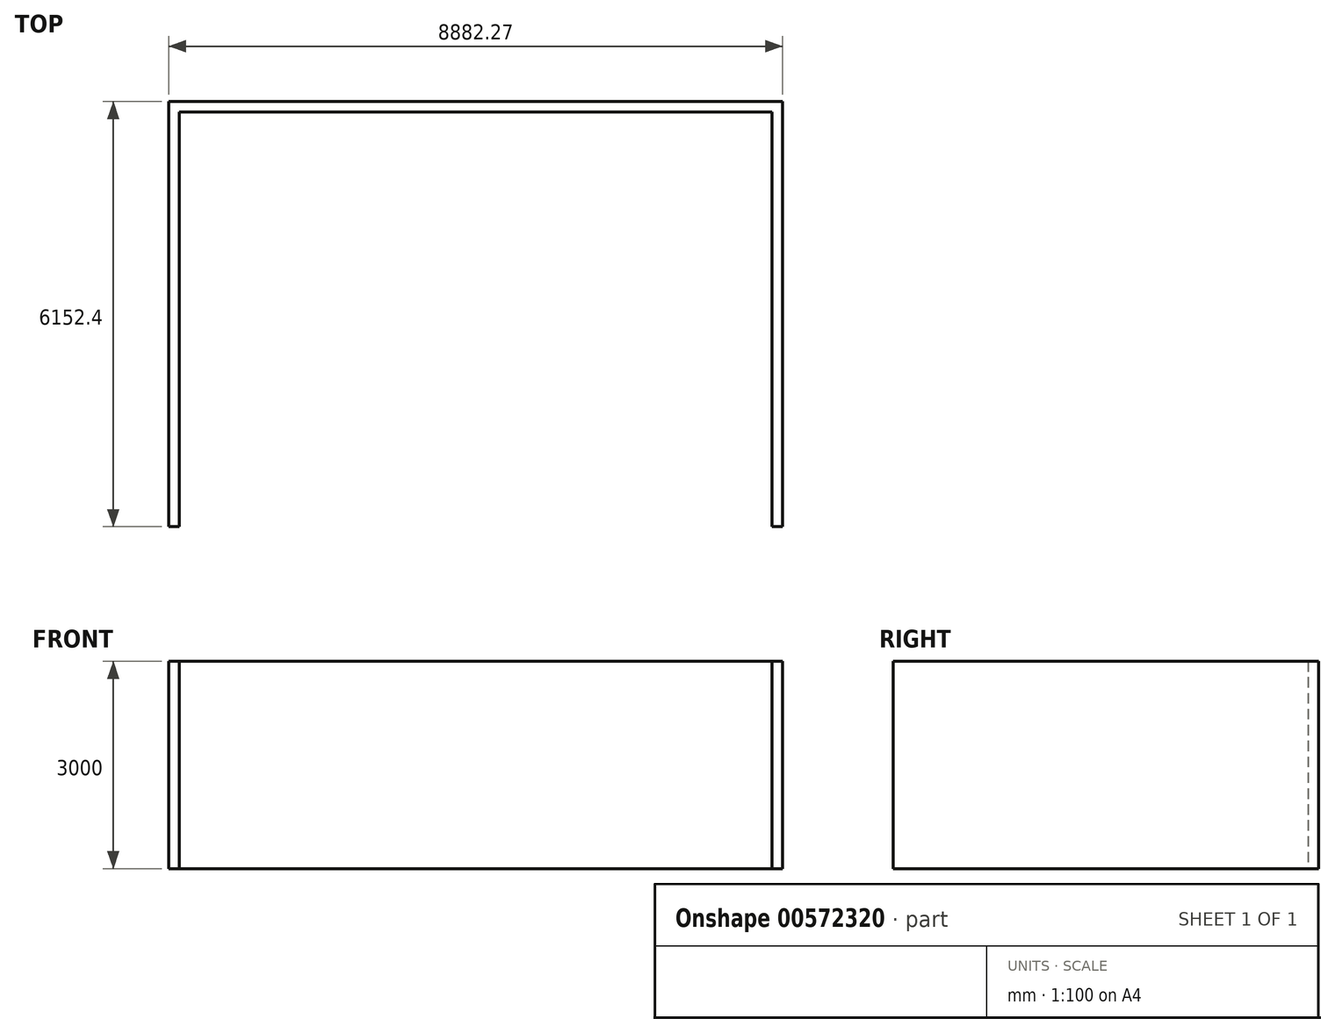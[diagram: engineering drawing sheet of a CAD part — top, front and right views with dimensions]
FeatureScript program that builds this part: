
annotation { "Feature Type Name" : "Feature", "Feature Type Description" : "" }
export const myFeature = defineFeature(function(context is Context, id is Id, definition is map)
    precondition{}
    {
        {
            var Q0;
            Q0=qCreatedBy(makeId("Top.planeOp"),FACE);
            var sketch = newSketch(context, id + "F0", { "sketchPlane" : qUnion([Q0])});
            skLineSegment(sketch, "E0", {"start": v(2645.54, -1227.66) * mm, "end": v(2645.54, 474.14) * mm});
            skLineSegment(sketch, "E1", {"start": v(2645.54, 474.14) * mm, "end": v(4186.83, 474.14) * mm});
            skLineSegment(sketch, "E2", {"start": v(4186.83, 474.14) * mm, "end": v(5204.59, -238.35) * mm});
            skLineSegment(sketch, "E3", {"start": v(5204.59, -238.35) * mm, "end": v(5204.59, -2140.25) * mm});
            skLineSegment(sketch, "E4", {"start": v(5204.59, -1302.05) * mm, "end": v(4417.19, -1302.05) * mm});
            skLineSegment(sketch, "E5", {"start": v(4417.19, -1302.05) * mm, "end": v(4417.19, -2140.25) * mm});
            skLineSegment(sketch, "E6", {"start": v(2645.54, -1227.66) * mm, "end": v(3458.34, -1227.66) * mm});
            skLineSegment(sketch, "E7", {"start": v(3458.34, -1227.66) * mm, "end": v(3458.34, -1354.66) * mm});
            skLineSegment(sketch, "E8", {"start": v(3458.34, -1354.66) * mm, "end": v(2489.79, -1354.66) * mm});
            skLineSegment(sketch, "E9", {"start": v(2489.79, -1227.66) * mm, "end": v(2489.79, -6410.36) * mm});
            skLineSegment(sketch, "E10", {"start": v(4417.19, -2140.25) * mm, "end": v(4544.19, -2140.25) * mm});
            skLineSegment(sketch, "E11", {"start": v(4544.19, -2140.25) * mm, "end": v(4544.19, -1431.88) * mm});
            skLineSegment(sketch, "E12", {"start": v(4417.19, -1431.88) * mm, "end": v(5204.59, -1431.88) * mm});
            skLineSegment(sketch, "E13", {"start": v(4780.3, -2140.25) * mm, "end": v(5334.59, -2140.25) * mm});
            skLineSegment(sketch, "E14", {"start": v(5334.59, -2140.25) * mm, "end": v(5334.59, -170.67) * mm});
            skLineSegment(sketch, "E15", {"start": v(4986.53, -4821.76) * mm, "end": v(7214.19, -6283.36) * mm});
            skLineSegment(sketch, "E16", {"start": v(7214.19, -6283.36) * mm, "end": v(9652.59, -6283.36) * mm});
            skLineSegment(sketch, "E17", {"start": v(9652.59, -6283.36) * mm, "end": v(9652.59, 1812.9) * mm});
            skLineSegment(sketch, "E18", {"start": v(9652.59, 1812.9) * mm, "end": v(8541.34, 1812.9) * mm});
            skLineSegment(sketch, "E19", {"start": v(8541.34, 1812.9) * mm, "end": v(8541.34, 5165.7) * mm});
            skLineSegment(sketch, "E20", {"start": v(8541.34, 5165.7) * mm, "end": v(7121.46, 5903.66) * mm});
            skLineSegment(sketch, "E21", {"start": v(7121.46, 5903.66) * mm, "end": v(5406.96, 5903.66) * mm});
            skLineSegment(sketch, "E22", {"start": v(5406.96, 5903.66) * mm, "end": v(4807.54, 4849.3) * mm});
            skLineSegment(sketch, "E23", {"start": v(4807.54, 4849.3) * mm, "end": v(4807.54, 3560.24) * mm});
            skLineSegment(sketch, "E24", {"start": v(4807.54, 3560.24) * mm, "end": v(-7773.83, 3560.24) * mm});
            skLineSegment(sketch, "E25", {"start": v(5334.59, -170.67) * mm, "end": v(4232.1, 601.14) * mm});
            skLineSegment(sketch, "E26", {"start": v(4232.1, 601.14) * mm, "end": v(97.26, 601.14) * mm});
            skLineSegment(sketch, "E27.bottom", {"start": v(4232.1, 1693.34) * mm, "end": v(5822.02, 1693.34) * mm});
            skLineSegment(sketch, "E27.top", {"start": v(4232.1, 1515.54) * mm, "end": v(5822.02, 1515.54) * mm});
            skLineSegment(sketch, "E27.left", {"start": v(4232.1, 1693.34) * mm, "end": v(4232.1, 1515.54) * mm});
            skLineSegment(sketch, "E27.right", {"start": v(5822.02, 1693.34) * mm, "end": v(5822.02, 1515.54) * mm});
            skLineSegment(sketch, "E28", {"start": v(97.26, 601.14) * mm, "end": v(-662.53, -46.43) * mm});
            skLineSegment(sketch, "E29", {"start": v(-662.53, -46.43) * mm, "end": v(-662.53, -888.34) * mm});
            skLineSegment(sketch, "E30", {"start": v(-662.53, -888.34) * mm, "end": v(-241.43, -1354.66) * mm});
            skLineSegment(sketch, "E31", {"start": v(2518.54, -1354.66) * mm, "end": v(1140.26, -1354.66) * mm});
            skPoint(sketch, "E32.orphan", {"position": v(-288.93, -1302.05) * mm});
            skLineSegment(sketch, "E33", {"start": v(2518.54, -1227.66) * mm, "end": v(1140.26, -1227.66) * mm});
            skLineSegment(sketch, "E34", {"start": v(-185, -1227.66) * mm, "end": v(-536.37, -838.55) * mm});
            skLineSegment(sketch, "E35", {"start": v(-536.37, -838.55) * mm, "end": v(-536.37, -105.77) * mm});
            skLineSegment(sketch, "E36", {"start": v(-536.37, -105.77) * mm, "end": v(144.04, 474.14) * mm});
            skLineSegment(sketch, "E37", {"start": v(144.04, 474.14) * mm, "end": v(2645.54, 474.14) * mm});
            skLineSegment(sketch, "E38", {"start": v(2518.54, 474.14) * mm, "end": v(2518.54, -6283.36) * mm});
            skLineSegment(sketch, "E39", {"start": v(4986.53, -4821.76) * mm, "end": v(2489.79, -4821.76) * mm});
            skLineSegment(sketch, "E40", {"start": v(-7773.83, -6283.36) * mm, "end": v(-7773.83, -4530.76) * mm});
            skLineSegment(sketch, "E41", {"start": v(-7773.83, -4530.76) * mm, "end": v(-6943.99, -4530.76) * mm});
            skLineSegment(sketch, "E42", {"start": v(-6943.99, -4530.76) * mm, "end": v(-6943.99, -3444.9) * mm});
            skLineSegment(sketch, "E43", {"start": v(-2809.3, -3444.9) * mm, "end": v(-7773.83, -3444.9) * mm});
            skLineSegment(sketch, "E44", {"start": v(-7773.83, -3444.9) * mm, "end": v(-7773.83, 3560.24) * mm});
            skLineSegment(sketch, "E45", {"start": v(97.26, 601.14) * mm, "end": v(144.04, 474.14) * mm});
            skLineSegment(sketch, "E46", {"start": v(-662.53, -46.43) * mm, "end": v(-536.37, -105.77) * mm});
            skLineSegment(sketch, "E47", {"start": v(-662.53, -888.34) * mm, "end": v(-536.37, -838.55) * mm});
            skLineSegment(sketch, "E48", {"start": v(-241.43, -1354.66) * mm, "end": v(-185, -1227.66) * mm});
            skLineSegment(sketch, "E49", {"start": v(4186.83, 474.14) * mm, "end": v(4232.1, 601.14) * mm});
            skLineSegment(sketch, "E50", {"start": v(5204.59, -238.35) * mm, "end": v(5334.59, -170.67) * mm});
            skLineSegment(sketch, "E51", {"start": v(485.77, -1354.66) * mm, "end": v(485.77, -1227.66) * mm});
            skLineSegment(sketch, "E52", {"start": v(1140.26, -1227.66) * mm, "end": v(1140.26, -1354.66) * mm});
            skPoint(sketch, "E52.endSnap0", {"position": v(1138.55, -1354.66) * mm});
            skLineSegment(sketch, "E53.trimOffspring", {"start": v(485.77, -1227.66) * mm, "end": v(-185, -1227.66) * mm});
            skLineSegment(sketch, "E54.trimOffspring", {"start": v(485.77, -1354.66) * mm, "end": v(-241.43, -1354.66) * mm});
            skLineSegment(sketch, "E55.0", {"start": v(4944.59, -4948.76) * mm, "end": v(2489.79, -4948.76) * mm});
            skLineSegment(sketch, "E55.1", {"start": v(-7900.83, -6410.36) * mm, "end": v(-7900.83, -4403.76) * mm});
            skLineSegment(sketch, "E55.2", {"start": v(-7900.83, -155.6) * mm, "end": v(-7900.83, 3687.24) * mm});
            skLineSegment(sketch, "E55.3", {"start": v(4680.54, 3687.24) * mm, "end": v(-7900.83, 3687.24) * mm});
            skLineSegment(sketch, "E55.4", {"start": v(9779.59, -6410.36) * mm, "end": v(9779.59, 1939.9) * mm});
            skLineSegment(sketch, "E55.5", {"start": v(6916.19, -6410.36) * mm, "end": v(9779.59, -6410.36) * mm});
            skLineSegment(sketch, "E55.8", {"start": v(9779.59, 1939.9) * mm, "end": v(8668.34, 1939.9) * mm});
            skLineSegment(sketch, "E55.9", {"start": v(8668.34, 1939.9) * mm, "end": v(8668.34, 5242.81) * mm});
            skLineSegment(sketch, "E55.10", {"start": v(8668.34, 5242.81) * mm, "end": v(7152.5, 6030.66) * mm});
            skLineSegment(sketch, "E55.11", {"start": v(7152.5, 6030.66) * mm, "end": v(5333.07, 6030.66) * mm});
            skLineSegment(sketch, "E55.12", {"start": v(5333.07, 6030.66) * mm, "end": v(4680.54, 4882.87) * mm});
            skLineSegment(sketch, "E55.13", {"start": v(4680.54, 4882.87) * mm, "end": v(4680.54, 3687.24) * mm});
            skLineSegment(sketch, "E56.0", {"start": v(-2809.3, -3571.9) * mm, "end": v(-7900.83, -3571.9) * mm});
            skLineSegment(sketch, "E56.1", {"start": v(-7070.99, -4403.76) * mm, "end": v(-7070.99, -3571.9) * mm});
            skLineSegment(sketch, "E56.2", {"start": v(-7900.83, -4403.76) * mm, "end": v(-7070.99, -4403.76) * mm});
            skLineSegment(sketch, "E57.trimOffspring", {"start": v(-7900.83, -3571.9) * mm, "end": v(-7900.83, -155.6) * mm});
            skLineSegment(sketch, "E58", {"start": v(-2682.3, 3560.24) * mm, "end": v(-2682.3, 1046.56) * mm});
            skLineSegment(sketch, "E59", {"start": v(-2682.3, 1046.56) * mm, "end": v(-2903.72, 1046.56) * mm});
            skLineSegment(sketch, "E60", {"start": v(-3749.48, 1173.56) * mm, "end": v(-3749.48, -282.6) * mm});
            skLineSegment(sketch, "E61", {"start": v(-3749.48, -155.6) * mm, "end": v(-3665.72, -155.6) * mm});
            skLineSegment(sketch, "E62", {"start": v(-2682.3, -155.6) * mm, "end": v(-2682.3, -4527.58) * mm});
            skLineSegment(sketch, "E63.0", {"start": v(-2809.3, -155.6) * mm, "end": v(-2809.3, -4527.58) * mm});
            skLineSegment(sketch, "E63.1", {"start": v(-2809.3, 3485.85) * mm, "end": v(-2809.3, 1046.56) * mm});
            skLineSegment(sketch, "E63.2", {"start": v(-2809.3, 1173.56) * mm, "end": v(-2903.72, 1173.56) * mm});
            skLineSegment(sketch, "E63.3", {"start": v(-3876.48, 1173.56) * mm, "end": v(-3876.48, -282.6) * mm});
            skLineSegment(sketch, "E63.4", {"start": v(-3876.48, -282.6) * mm, "end": v(-3665.72, -282.6) * mm});
            skLineSegment(sketch, "E64", {"start": v(-3876.48, 445.47) * mm, "end": v(-7773.83, 445.47) * mm});
            skLineSegment(sketch, "E65", {"start": v(-7773.83, 572.47) * mm, "end": v(-3876.48, 572.47) * mm});
            skLineSegment(sketch, "E66", {"start": v(-5355.07, -3571.9) * mm, "end": v(-5355.07, -4530.76) * mm});
            skLineSegment(sketch, "E67", {"start": v(-5355.07, -4530.76) * mm, "end": v(-5228.07, -4530.76) * mm});
            skLineSegment(sketch, "E68", {"start": v(-5228.07, -4530.76) * mm, "end": v(-5228.07, -3571.9) * mm});
            skLineSegment(sketch, "E69", {"start": v(-2809.3, -4527.58) * mm, "end": v(-2682.3, -4527.58) * mm});
            skLineSegment(sketch, "E70", {"start": v(-2809.3, -5232.43) * mm, "end": v(-2682.3, -5232.43) * mm});
            skLineSegment(sketch, "E71.trimOffspring", {"start": v(-2682.3, -5232.43) * mm, "end": v(-2682.3, -6283.36) * mm});
            skLineSegment(sketch, "E72.trimOffspring", {"start": v(-2809.3, -5232.43) * mm, "end": v(-2809.3, -6283.36) * mm});
            skLineSegment(sketch, "E73", {"start": v(-3665.72, 1173.56) * mm, "end": v(-3665.72, 1046.56) * mm});
            skLineSegment(sketch, "E74", {"start": v(-2903.72, 1173.56) * mm, "end": v(-2903.72, 1046.56) * mm});
            skLineSegment(sketch, "E75.trimOffspring", {"start": v(-3665.72, 1173.56) * mm, "end": v(-3876.48, 1173.56) * mm});
            skLineSegment(sketch, "E76.trimOffspring", {"start": v(-3665.72, 1046.56) * mm, "end": v(-3749.48, 1046.56) * mm});
            skLineSegment(sketch, "E77.trimOffspring", {"start": v(-2903.72, -155.6) * mm, "end": v(-2682.3, -155.6) * mm});
            skLineSegment(sketch, "E78.trimOffspring", {"start": v(-2903.72, -282.6) * mm, "end": v(-2809.3, -282.6) * mm});
            skLineSegment(sketch, "E79.trimOffspring", {"start": v(-2903.72, -155.6) * mm, "end": v(-2903.72, -282.6) * mm});
            skLineSegment(sketch, "E80.trimOffspring", {"start": v(-3665.72, -155.6) * mm, "end": v(-3665.72, -282.6) * mm});
            skLineSegment(sketch, "E81", {"start": v(-2682.3, 1227.1) * mm, "end": v(-867.36, 1227.1) * mm});
            skLineSegment(sketch, "E82", {"start": v(1803.51, 1227.1) * mm, "end": v(2694.47, 1951.7) * mm});
            skLineSegment(sketch, "E83", {"start": v(2694.47, 1951.7) * mm, "end": v(2694.47, 2417.7) * mm});
            skLineSegment(sketch, "E84.0", {"start": v(2567.47, 2012.12) * mm, "end": v(2567.47, 2417.7) * mm});
            skLineSegment(sketch, "E84.1", {"start": v(1758.39, 1354.1) * mm, "end": v(2567.47, 2012.12) * mm});
            skLineSegment(sketch, "E84.2", {"start": v(-2666.54, 1354.1) * mm, "end": v(-867.36, 1354.1) * mm});
            skLineSegment(sketch, "E85", {"start": v(2567.47, 3179.7) * mm, "end": v(2694.47, 3179.7) * mm});
            skLineSegment(sketch, "E86", {"start": v(2567.47, 2417.7) * mm, "end": v(2694.47, 2417.7) * mm});
            skLineSegment(sketch, "E87.trimOffspring", {"start": v(2694.47, 3179.7) * mm, "end": v(2694.47, 3560.24) * mm});
            skLineSegment(sketch, "E88.trimOffspring", {"start": v(2567.47, 3179.7) * mm, "end": v(2567.47, 3485.85) * mm});
            skLineSegment(sketch, "E89", {"start": v(529.73, 3560.24) * mm, "end": v(529.73, 1354.1) * mm});
            skLineSegment(sketch, "E90.0", {"start": v(402.73, 3485.85) * mm, "end": v(402.73, 1354.1) * mm});
            skLineSegment(sketch, "E91", {"start": v(-867.36, 1354.1) * mm, "end": v(-867.36, 1227.1) * mm});
            skLineSegment(sketch, "E92", {"start": v(-105.36, 1354.1) * mm, "end": v(-105.36, 1227.1) * mm});
            skLineSegment(sketch, "E93.trimOffspring", {"start": v(-105.36, 1354.1) * mm, "end": v(1758.39, 1354.1) * mm});
            skLineSegment(sketch, "E94.trimOffspring", {"start": v(-105.36, 1227.1) * mm, "end": v(1803.51, 1227.1) * mm});
            skLineSegment(sketch, "E95", {"start": v(2567.47, 2012.12) * mm, "end": v(2694.47, 1951.7) * mm});
            skLineSegment(sketch, "E96", {"start": v(1758.39, 1354.1) * mm, "end": v(1803.51, 1227.1) * mm});
            skLineSegment(sketch, "E97", {"start": v(2489.79, -6410.36) * mm, "end": v(-7900.83, -6410.36) * mm});
            skLineSegment(sketch, "E98.trimOffspring", {"start": v(2489.79, -6283.36) * mm, "end": v(-7900.83, -6283.36) * mm});
            skLineSegment(sketch, "E99.bottom", {"start": v(-3876.48, -282.6) * mm, "end": v(-7773.83, -282.6) * mm});
            skLineSegment(sketch, "E99.top", {"start": v(-3876.48, -155.6) * mm, "end": v(-7773.83, -155.6) * mm});
            skLineSegment(sketch, "E99.left", {"start": v(-3876.48, -282.6) * mm, "end": v(-3876.48, -155.6) * mm});
            skLineSegment(sketch, "E99.right", {"start": v(-7773.83, -282.6) * mm, "end": v(-7773.83, -155.6) * mm});
            skLineSegment(sketch, "E100", {"start": v(2489.79, -6410.36) * mm, "end": v(2489.79, -7019.96) * mm});
            skLineSegment(sketch, "E101", {"start": v(2489.79, -7019.96) * mm, "end": v(-8510.43, -7019.96) * mm});
            skLineSegment(sketch, "E102", {"start": v(-8510.43, -7019.96) * mm, "end": v(-8510.43, 3687.24) * mm});
            skLineSegment(sketch, "E103", {"start": v(-8510.43, 3687.24) * mm, "end": v(-7900.83, 3687.24) * mm});
            skLineSegment(sketch, "E104", {"start": v(-85.36, 3687.24) * mm, "end": v(-85.36, 9839.64) * mm});
            skLineSegment(sketch, "E105", {"start": v(-8510.43, 3687.24) * mm, "end": v(-8967.63, 3687.24) * mm});
            skLineSegment(sketch, "E106", {"start": v(-8967.63, 3687.24) * mm, "end": v(-8967.63, 9839.64) * mm});
            skLineSegment(sketch, "E107", {"start": v(-8967.63, 9839.64) * mm, "end": v(-85.36, 9839.64) * mm});
            skLineSegment(sketch, "E108.1", {"start": v(-8815.23, 9687.24) * mm, "end": v(-237.76, 9687.24) * mm});
            skLineSegment(sketch, "E108.2", {"start": v(-8815.23, 3687.24) * mm, "end": v(-8815.23, 9687.24) * mm});
            skLineSegment(sketch, "E109.trimOffspring", {"start": v(-237.76, 3687.24) * mm, "end": v(-237.76, 9687.24) * mm});
            skLineSegment(sketch, "E110.trimOffspring", {"start": v(4944.59, -4948.76) * mm, "end": v(6916.19, -6410.36) * mm});
            skSolve(sketch);
        }
        {
            var Q0;
            {var subQ5=sQuery(id+"F0.wireOp",EDGE,"E104");Q0=makeQuery(id+"F0.imprint","IMPRINT",FACE,{"disambiguationData":[TD([[makeQuery(id+"F0.imprint","IMPRINT",EDGE,{"derivedFrom":subQ5}),1.0]])]});}
            extrude(context, id + "F1", {"entities" : qUnion([Q0]), "depth" : 3000 * mm, "offsetDistance" : 25 * mm});
        }
    });
